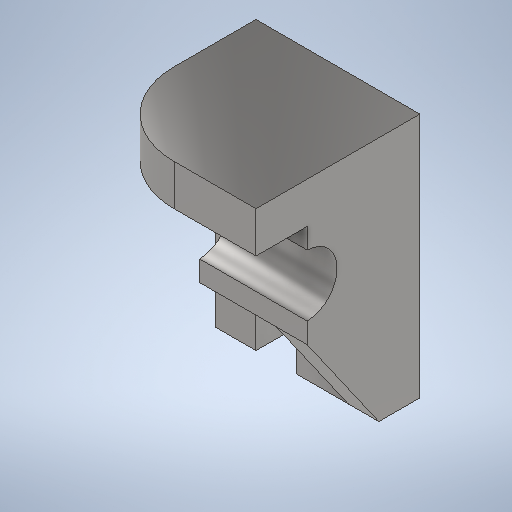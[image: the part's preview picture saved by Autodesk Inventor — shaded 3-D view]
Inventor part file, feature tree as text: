
AUTODESK INVENTOR PART (.ipt)
format: ipt  version: 2025.2 (Build 292293000, 293)  size: 289,280 bytes
history: native  units: in
note: dims shown in document units (in); Inventor stores cm internally (conversion verified against a paired STEP export)
features: sketch x5, extrude x4, plane x2, rib x1
ambient origin geometry x8: Origin, YZ Plane, XZ Plane, XY Plane, X Axis, Y Axis, Z Axis, Center Point
bodies: Solid1 (feature_tree)
feature tree (12):
  extrude  "Extrusion1"  Depth=3.7795in
  plane  "Work Plane1"
  extrude  "Extrusion2"  Depth=0.7874in
  extrude  "Extrusion3"  Depth=0.6299in TaperAngle=0.0deg
  extrude  "Extrusion4"  Depth=1.8898in
  plane  "Work Plane2"
  rib  "Rib1"
  sketch  "Sketch1"  dims[d0=2.5197in d1=3.7795in]
  sketch  "Sketch2"  dims[d2=0.6299in d3=0.7874in]
  sketch  "Sketch3"  dims[d4=0.6299in d5=0.6299in d6=0.0in]
  sketch  "Sketch4"  dims[d7=1.8898in d8=1.8898in]
  sketch  "Sketch5"  dims[d9=1.2598in d10=0.6299in d11=0.0in d12=1.6535in d13=1.5748in d14=0.8661in d15=0.0in d16=1.1024in d17=0.0in d20=0.4726in d21=1.6535in d22=0.0in d23=0.7874in d24=0.0394in d25=0.4724in d26=0.0in d27=0.0in d28=0.0394in d29=0.0394in]
